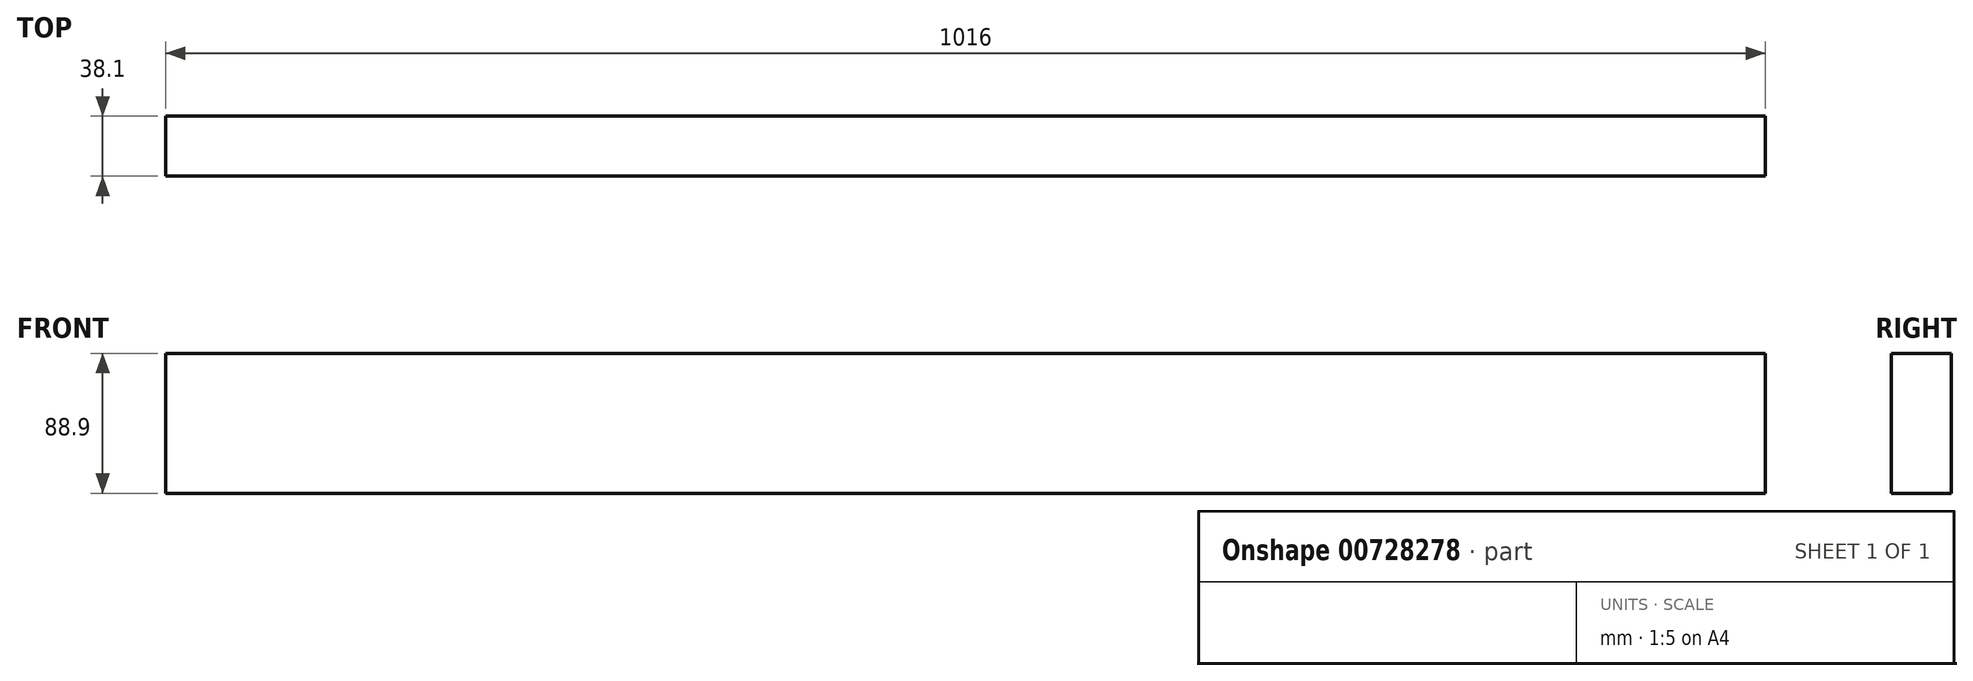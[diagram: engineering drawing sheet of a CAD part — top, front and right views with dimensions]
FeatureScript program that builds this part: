
annotation { "Feature Type Name" : "Feature", "Feature Type Description" : "" }
export const myFeature = defineFeature(function(context is Context, id is Id, definition is map)
    precondition{}
    {
        {
            var Q0;
            Q0=qCreatedBy(makeId("Front.planeOp"),FACE);
            var sketch = newSketch(context, id + "F0", { "sketchPlane" : qUnion([Q0])});
            skLineSegment(sketch, "E0.bottom", {"start": v(-508, -44.45) * mm, "end": v(508, -44.45) * mm});
            skLineSegment(sketch, "E0.top", {"start": v(-508, 44.45) * mm, "end": v(508, 44.45) * mm});
            skLineSegment(sketch, "E0.left", {"start": v(-508, -44.45) * mm, "end": v(-508, 44.45) * mm});
            skLineSegment(sketch, "E0.right", {"start": v(508, -44.45) * mm, "end": v(508, 44.45) * mm});
            skPoint(sketch, "E0.middle", {"position": v(0, 0) * mm});
            skSolve(sketch);
        }
        {
            var Q0;
            Q0=qSketchRegion(id+"F0",true);
            extrude(context, id + "F1", {"entities" : qUnion([Q0]), "depth" : 38.1 * mm, "offsetDistance" : 25.4 * mm});
        }
    });
